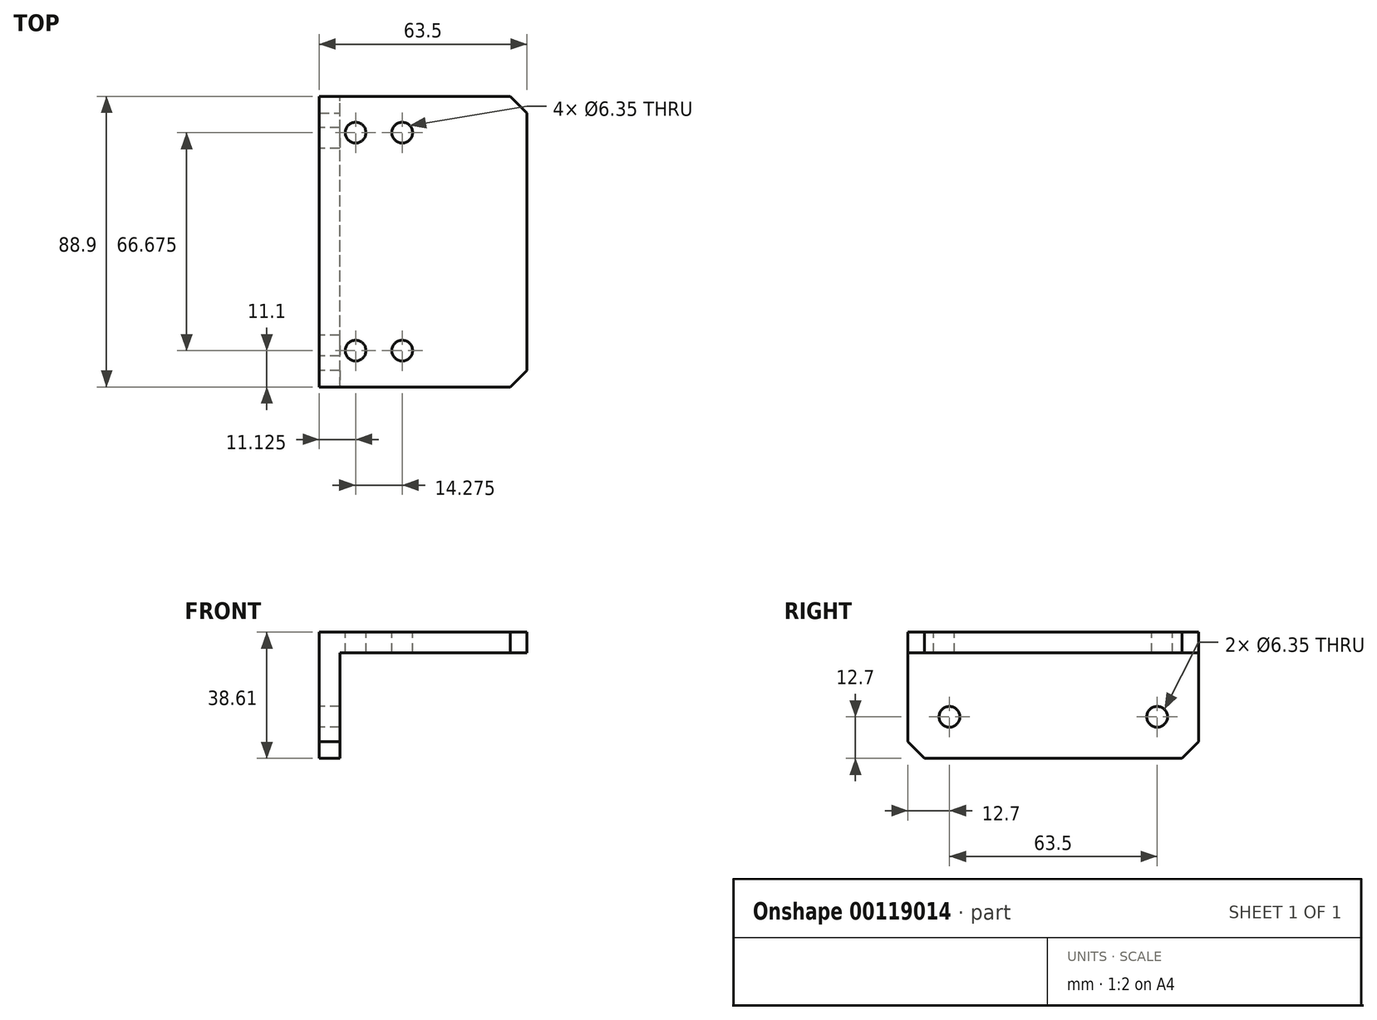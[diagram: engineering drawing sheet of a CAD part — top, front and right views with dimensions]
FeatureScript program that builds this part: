
annotation { "Feature Type Name" : "Feature", "Feature Type Description" : "" }
export const myFeature = defineFeature(function(context is Context, id is Id, definition is map)
    precondition{}
    {
        {
            var Q0;
            Q0=qCreatedBy(makeId("Front.planeOp"),FACE);
            var sketch = newSketch(context, id + "F0", { "sketchPlane" : qUnion([Q0])});
            skLineSegment(sketch, "E0", {"start": v(0, 0) * mm, "end": v(0, 38.6) * mm});
            skLineSegment(sketch, "E1", {"start": v(0, 38.6) * mm, "end": v(63.5, 38.6) * mm});
            skLineSegment(sketch, "E2", {"start": v(63.5, 38.6) * mm, "end": v(63.5, 32.26) * mm});
            skLineSegment(sketch, "E3", {"start": v(63.5, 32.26) * mm, "end": v(6.35, 32.26) * mm});
            skLineSegment(sketch, "E4", {"start": v(6.35, 32.26) * mm, "end": v(6.35, 0) * mm});
            skLineSegment(sketch, "E5", {"start": v(6.35, 0) * mm, "end": v(0, 0) * mm});
            skSolve(sketch);
        }
        {
            var Q0;
            Q0 = qSketchRegion(id + "F0", true);
            extrude(context, id + "F1", {"entities" : qUnion([Q0]), "depth" : 88.9 * mm});
        }
        {
            var Q0;
            Q0=qCreatedBy(makeId("Right.planeOp"),FACE);
            var sketch = newSketch(context, id + "F2", { "sketchPlane" : qUnion([Q0])});
            skPoint(sketch, "E6", {"position": v(-76.2, 12.7) * mm});
            skPoint(sketch, "E7", {"position": v(-12.7, 12.7) * mm});
            skSolve(sketch);
        }
        {
            var Q0;
            Q0=sQuery(id+"F2.wireOp",VERTEX,"E6");
            var Q1;
            Q1=sQuery(id+"F2.wireOp",VERTEX,"E7");
            var Q2;
            Q2=makeQuery(id+"F1.opExtrude","SWEPT_BODY",BODY,{"disambiguationData":[OSD([sQuery(id+"F0.wireOp",EDGE,"E0"),sQuery(id+"F0.wireOp",EDGE,"E1"),sQuery(id+"F0.wireOp",EDGE,"E2"),sQuery(id+"F0.wireOp",EDGE,"E3"),sQuery(id+"F0.wireOp",EDGE,"E4"),sQuery(id+"F0.wireOp",EDGE,"E5")])]});
            hole(context, id + "F3", {"style" : HoleStyle.SIMPLE, "endStyle" : HoleEndStyle.THROUGH, "oppositeDirection" : true, "holeDiameter" : 6.35 * mm, "locations" : qUnion([Q0, Q1]), "scope" : qUnion([Q2]), "isTappedThrough" : true});
        }
        {
            var Q0;
            Q0=makeQuery(id+"F1.opExtrude","CAP_EDGE",EDGE,{"disambiguationData":[OSD([sQuery(id+"F0.wireOp",EDGE,"E2")])],"isStart":true});
            var Q1;
            Q1=makeQuery(id+"F1.opExtrude","CAP_EDGE",EDGE,{"disambiguationData":[OSD([sQuery(id+"F0.wireOp",EDGE,"E2")])],"isStart":false});
            var Q2;
            Q2=makeQuery(id+"F1.opExtrude","CAP_EDGE",EDGE,{"disambiguationData":[OSD([sQuery(id+"F0.wireOp",EDGE,"E5")])],"isStart":false});
            var Q3;
            Q3=makeQuery(id+"F1.opExtrude","CAP_EDGE",EDGE,{"disambiguationData":[OSD([sQuery(id+"F0.wireOp",EDGE,"E5")])],"isStart":true});
            chamfer(context, id + "F4", {"entities" : qUnion([Q0, Q1, Q2, Q3]), "width" : 5.08 * mm, "tangentPropagation" : true});
        }
        {
            var Q0;
            Q0=makeQuery(id+"F1.opExtrude","SWEPT_FACE",FACE,{"disambiguationData":[OSD([sQuery(id+"F0.wireOp",EDGE,"E1")])]});
            var sketch = newSketch(context, id + "F5", { "sketchPlane" : qUnion([Q0])});
            skPoint(sketch, "E8", {"position": v(11.13, -11.13) * mm});
            skPoint(sketch, "E9", {"position": v(25.4, -11.13) * mm});
            skPoint(sketch, "E10", {"position": v(11.13, -77.8) * mm});
            skPoint(sketch, "E11", {"position": v(25.4, -77.8) * mm});
            skSolve(sketch);
        }
        {
            var Q0;
            Q0=sQuery(id+"F5.wireOp",VERTEX,"E9");
            var Q1;
            Q1=sQuery(id+"F5.wireOp",VERTEX,"E8");
            var Q2;
            Q2=sQuery(id+"F5.wireOp",VERTEX,"E10");
            var Q3;
            Q3=sQuery(id+"F5.wireOp",VERTEX,"E11");
            var Q4;
            Q4=makeQuery(id+"F1.opExtrude","SWEPT_BODY",BODY,{"disambiguationData":[OSD([sQuery(id+"F0.wireOp",EDGE,"E0"),sQuery(id+"F0.wireOp",EDGE,"E1"),sQuery(id+"F0.wireOp",EDGE,"E2"),sQuery(id+"F0.wireOp",EDGE,"E3"),sQuery(id+"F0.wireOp",EDGE,"E4"),sQuery(id+"F0.wireOp",EDGE,"E5")])]});
            hole(context, id + "F6", {"style" : HoleStyle.SIMPLE, "endStyle" : HoleEndStyle.THROUGH, "holeDiameter" : 6.35 * mm, "locations" : qUnion([Q0, Q1, Q2, Q3]), "scope" : qUnion([Q4]), "isTappedThrough" : true});
        }
    });
